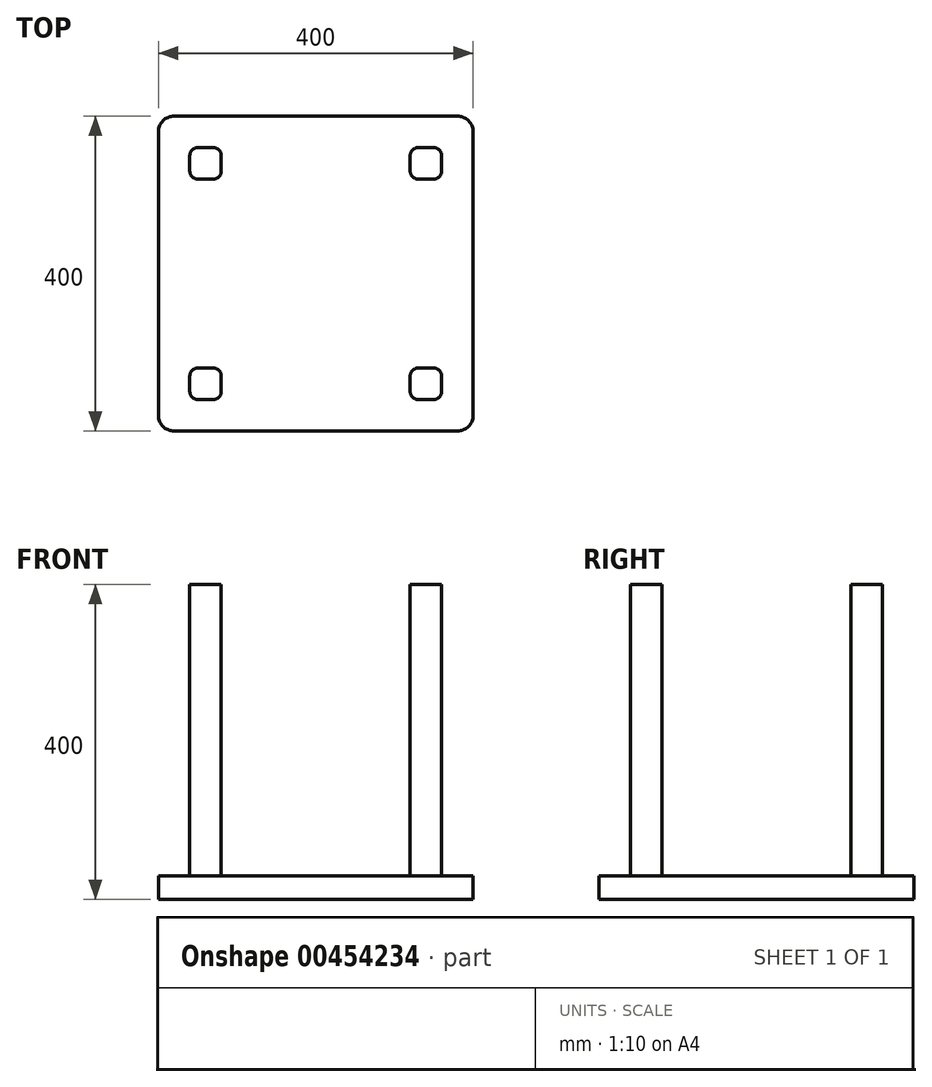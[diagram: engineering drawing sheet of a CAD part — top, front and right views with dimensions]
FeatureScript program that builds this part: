
annotation { "Feature Type Name" : "Feature", "Feature Type Description" : "" }
export const myFeature = defineFeature(function(context is Context, id is Id, definition is map)
    precondition{}
    {
        {
            var Q0;
            Q0=qCreatedBy(makeId("Top.planeOp"),FACE);
            var sketch = newSketch(context, id + "F0", { "sketchPlane" : qUnion([Q0])});
            skLineSegment(sketch, "E0.bottom", {"start": v(-202.46, 220.73) * mm, "end": v(157.54, 220.73) * mm});
            skLineSegment(sketch, "E0.top", {"start": v(-202.46, -179.27) * mm, "end": v(157.54, -179.27) * mm});
            skLineSegment(sketch, "E0.left", {"start": v(-222.46, 200.73) * mm, "end": v(-222.46, -159.27) * mm});
            skLineSegment(sketch, "E0.right", {"start": v(177.54, 200.73) * mm, "end": v(177.54, -159.27) * mm});
            skPoint(sketch, "E1.visualSharp", {"position": v(-222.46, 220.73) * mm});
            skArc(sketch, "E1.filletArc", {"start": v(-202.46, 220.73) * mm, "mid": v(-216.6, 214.87) * mm, "end": v(-222.46, 200.73) * mm});
            skPoint(sketch, "E2.visualSharp", {"position": v(177.54, 220.73) * mm});
            skArc(sketch, "E2.filletArc", {"start": v(177.54, 200.73) * mm, "mid": v(171.68, 214.87) * mm, "end": v(157.54, 220.73) * mm});
            skPoint(sketch, "E3.visualSharp", {"position": v(177.54, -179.27) * mm});
            skArc(sketch, "E3.filletArc", {"start": v(157.54, -179.27) * mm, "mid": v(171.68, -173.41) * mm, "end": v(177.54, -159.27) * mm});
            skPoint(sketch, "E4.visualSharp", {"position": v(-222.46, -179.27) * mm});
            skArc(sketch, "E4.filletArc", {"start": v(-222.46, -159.27) * mm, "mid": v(-216.6, -173.41) * mm, "end": v(-202.46, -179.27) * mm});
            skSolve(sketch);
        }
        {
            var Q0;
            Q0=makeQuery(id+"F0.imprint","IMPRINT",FACE,{"disambiguationData":[TD([[makeQuery(id+"F0.imprint","IMPRINT",EDGE,{"derivedFrom":sQuery(id+"F0.wireOp",EDGE,"E0.bottom")}),-1.0]])]});
            extrude(context, id + "F1", {"entities" : qUnion([Q0]), "depth" : 30 * mm});
        }
        {
            var Q0;
            Q0=makeQuery(id+"F1.opExtrude","CAP_FACE",FACE,{"disambiguationData":[OSD([sQuery(id+"F0.wireOp",EDGE,"E0.bottom"),sQuery(id+"F0.wireOp",EDGE,"E0.top"),sQuery(id+"F0.wireOp",EDGE,"E0.left"),sQuery(id+"F0.wireOp",EDGE,"E0.right"),sQuery(id+"F0.wireOp",EDGE,"E1.filletArc"),sQuery(id+"F0.wireOp",EDGE,"E2.filletArc"),sQuery(id+"F0.wireOp",EDGE,"E3.filletArc"),sQuery(id+"F0.wireOp",EDGE,"E4.filletArc")])],"isStart":false});
            var sketch = newSketch(context, id + "F2", { "sketchPlane" : qUnion([Q0])});
            skLineSegment(sketch, "E5.bottom", {"start": v(-172.46, 180.73) * mm, "end": v(-152.46, 180.73) * mm});
            skLineSegment(sketch, "E5.top", {"start": v(-172.46, 140.73) * mm, "end": v(-152.46, 140.73) * mm});
            skLineSegment(sketch, "E5.left", {"start": v(-182.46, 170.73) * mm, "end": v(-182.46, 150.73) * mm});
            skLineSegment(sketch, "E5.right", {"start": v(-142.46, 170.73) * mm, "end": v(-142.46, 150.73) * mm});
            skLineSegment(sketch, "E6.bottom", {"start": v(107.54, 180.73) * mm, "end": v(127.54, 180.73) * mm});
            skLineSegment(sketch, "E6.top", {"start": v(107.54, 140.73) * mm, "end": v(127.54, 140.73) * mm});
            skLineSegment(sketch, "E6.left", {"start": v(97.54, 170.73) * mm, "end": v(97.54, 150.73) * mm});
            skLineSegment(sketch, "E6.right", {"start": v(137.54, 170.73) * mm, "end": v(137.54, 150.73) * mm});
            skLineSegment(sketch, "E7.bottom", {"start": v(-172.46, -99.27) * mm, "end": v(-152.46, -99.27) * mm});
            skLineSegment(sketch, "E7.top", {"start": v(-172.46, -139.27) * mm, "end": v(-152.46, -139.27) * mm});
            skLineSegment(sketch, "E7.left", {"start": v(-182.46, -109.27) * mm, "end": v(-182.46, -129.27) * mm});
            skLineSegment(sketch, "E7.right", {"start": v(-142.46, -109.27) * mm, "end": v(-142.46, -129.27) * mm});
            skLineSegment(sketch, "E8.bottom", {"start": v(107.54, -99.27) * mm, "end": v(127.54, -99.27) * mm});
            skLineSegment(sketch, "E8.top", {"start": v(107.54, -139.27) * mm, "end": v(127.54, -139.27) * mm});
            skLineSegment(sketch, "E8.left", {"start": v(97.54, -109.27) * mm, "end": v(97.54, -129.27) * mm});
            skLineSegment(sketch, "E8.right", {"start": v(137.54, -109.27) * mm, "end": v(137.54, -129.27) * mm});
            skPoint(sketch, "E9.visualSharp", {"position": v(-182.46, 180.73) * mm});
            skArc(sketch, "E9.filletArc", {"start": v(-172.46, 180.73) * mm, "mid": v(-179.53, 177.8) * mm, "end": v(-182.46, 170.73) * mm});
            skPoint(sketch, "E10.visualSharp", {"position": v(-142.46, 180.73) * mm});
            skArc(sketch, "E10.filletArc", {"start": v(-142.46, 170.73) * mm, "mid": v(-145.39, 177.8) * mm, "end": v(-152.46, 180.73) * mm});
            skPoint(sketch, "E11.visualSharp", {"position": v(-142.46, 140.73) * mm});
            skArc(sketch, "E11.filletArc", {"start": v(-152.46, 140.73) * mm, "mid": v(-145.39, 143.66) * mm, "end": v(-142.46, 150.73) * mm});
            skPoint(sketch, "E12.visualSharp", {"position": v(-182.46, 140.73) * mm});
            skArc(sketch, "E12.filletArc", {"start": v(-182.46, 150.73) * mm, "mid": v(-179.53, 143.66) * mm, "end": v(-172.46, 140.73) * mm});
            skPoint(sketch, "E13.visualSharp", {"position": v(97.54, 180.73) * mm});
            skArc(sketch, "E13.filletArc", {"start": v(107.54, 180.73) * mm, "mid": v(100.47, 177.8) * mm, "end": v(97.54, 170.73) * mm});
            skPoint(sketch, "E14.visualSharp", {"position": v(137.54, 180.73) * mm});
            skArc(sketch, "E14.filletArc", {"start": v(137.54, 170.73) * mm, "mid": v(134.61, 177.8) * mm, "end": v(127.54, 180.73) * mm});
            skPoint(sketch, "E15.visualSharp", {"position": v(137.54, 140.73) * mm});
            skArc(sketch, "E15.filletArc", {"start": v(127.54, 140.73) * mm, "mid": v(134.61, 143.66) * mm, "end": v(137.54, 150.73) * mm});
            skPoint(sketch, "E16.visualSharp", {"position": v(97.54, 140.73) * mm});
            skArc(sketch, "E16.filletArc", {"start": v(97.54, 150.73) * mm, "mid": v(100.47, 143.66) * mm, "end": v(107.54, 140.73) * mm});
            skPoint(sketch, "E17.visualSharp", {"position": v(97.54, -99.27) * mm});
            skArc(sketch, "E17.filletArc", {"start": v(107.54, -99.27) * mm, "mid": v(100.47, -102.2) * mm, "end": v(97.54, -109.27) * mm});
            skPoint(sketch, "E18.visualSharp", {"position": v(137.54, -99.27) * mm});
            skArc(sketch, "E18.filletArc", {"start": v(137.54, -109.27) * mm, "mid": v(134.61, -102.2) * mm, "end": v(127.54, -99.27) * mm});
            skPoint(sketch, "E19.visualSharp", {"position": v(137.54, -139.27) * mm});
            skArc(sketch, "E19.filletArc", {"start": v(127.54, -139.27) * mm, "mid": v(134.61, -136.34) * mm, "end": v(137.54, -129.27) * mm});
            skPoint(sketch, "E20.visualSharp", {"position": v(97.54, -139.27) * mm});
            skArc(sketch, "E20.filletArc", {"start": v(97.54, -129.27) * mm, "mid": v(100.47, -136.34) * mm, "end": v(107.54, -139.27) * mm});
            skPoint(sketch, "E21.visualSharp", {"position": v(-142.46, -139.27) * mm});
            skArc(sketch, "E21.filletArc", {"start": v(-152.46, -139.27) * mm, "mid": v(-145.39, -136.34) * mm, "end": v(-142.46, -129.27) * mm});
            skPoint(sketch, "E22.visualSharp", {"position": v(-142.46, -99.27) * mm});
            skArc(sketch, "E22.filletArc", {"start": v(-142.46, -109.27) * mm, "mid": v(-145.39, -102.2) * mm, "end": v(-152.46, -99.27) * mm});
            skPoint(sketch, "E23.visualSharp", {"position": v(-182.46, -99.27) * mm});
            skArc(sketch, "E23.filletArc", {"start": v(-172.46, -99.27) * mm, "mid": v(-179.53, -102.2) * mm, "end": v(-182.46, -109.27) * mm});
            skPoint(sketch, "E24.visualSharp", {"position": v(-182.46, -139.27) * mm});
            skArc(sketch, "E24.filletArc", {"start": v(-182.46, -129.27) * mm, "mid": v(-179.53, -136.34) * mm, "end": v(-172.46, -139.27) * mm});
            skSolve(sketch);
        }
        {
            var Q0;
            Q0=makeQuery(id+"F2.imprint","IMPRINT",FACE,{"disambiguationData":[TD([[makeQuery(id+"F2.imprint","IMPRINT",EDGE,{"derivedFrom":sQuery(id+"F2.wireOp",EDGE,"E5.bottom")}),-1.0]])]});
            var Q1;
            Q1=makeQuery(id+"F2.imprint","IMPRINT",FACE,{"disambiguationData":[TD([[makeQuery(id+"F2.imprint","IMPRINT",EDGE,{"derivedFrom":sQuery(id+"F2.wireOp",EDGE,"E6.bottom")}),-1.0]])]});
            var Q2;
            Q2=makeQuery(id+"F2.imprint","IMPRINT",FACE,{"disambiguationData":[TD([[makeQuery(id+"F2.imprint","IMPRINT",EDGE,{"derivedFrom":sQuery(id+"F2.wireOp",EDGE,"E8.bottom")}),-1.0]])]});
            var Q3;
            Q3=makeQuery(id+"F2.imprint","IMPRINT",FACE,{"disambiguationData":[TD([[makeQuery(id+"F2.imprint","IMPRINT",EDGE,{"derivedFrom":sQuery(id+"F2.wireOp",EDGE,"E7.bottom")}),-1.0]])]});
            extrude(context, id + "F3", {"entities" : qUnion([Q0, Q1, Q2, Q3]), "operationType" : NewBodyOperationType.ADD, "depth" : 370 * mm});
        }
    });
